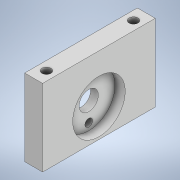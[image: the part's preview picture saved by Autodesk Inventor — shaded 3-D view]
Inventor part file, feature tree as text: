
AUTODESK INVENTOR PART (.ipt)
format: ipt  version: 2020 (Build 240168000, 168)  size: 140,800 bytes
history: native  units: mm
features: extrude x3, sketch x2, other x1, projected_geometry x1
ambient origin geometry x8: Origin, YZ Plane, XZ Plane, XY Plane, X Axis, Y Axis, Z Axis, Center Point
bodies: Body1 (feature_tree)
feature tree (7):
  other  "Твердое тело1"
  extrude  "Выдавливание1"  Depth=44.0mm
  sketch  "Эскиз2"
  extrude  "Выдавливание2"  Depth=7.0mm
  extrude  "Выдавливание3"  Depth=3.5mm
  sketch  "Эскиз1"
  projected_geometry  "Спроецированная петля1"
